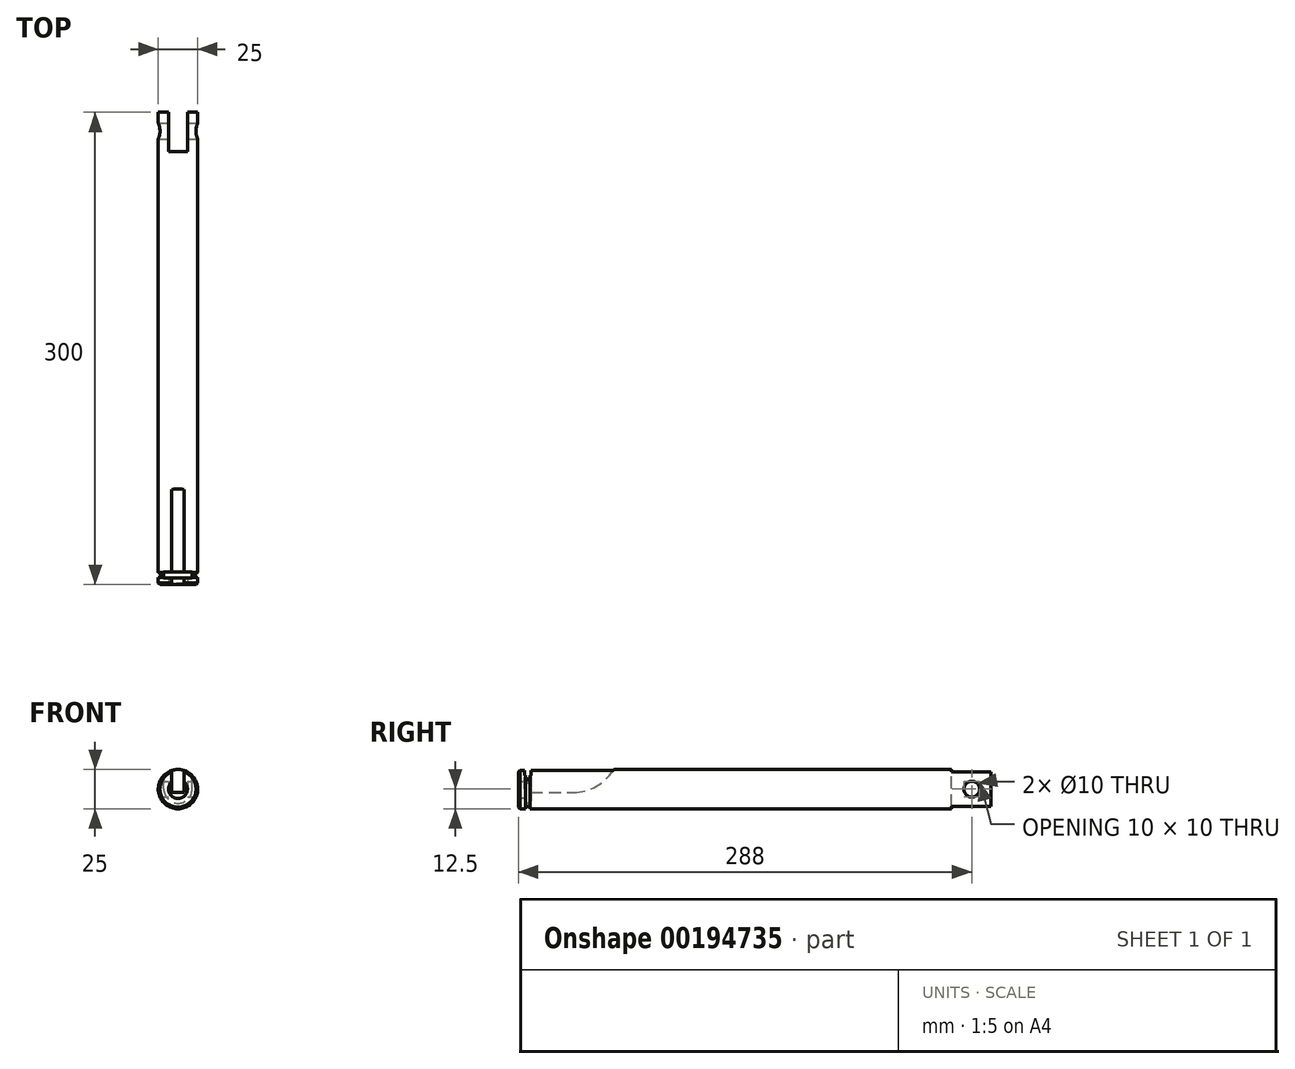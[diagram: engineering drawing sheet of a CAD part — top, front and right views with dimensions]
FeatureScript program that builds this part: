
annotation { "Feature Type Name" : "Feature", "Feature Type Description" : "" }
export const myFeature = defineFeature(function(context is Context, id is Id, definition is map)
    precondition{}
    {
        {
            var Q0;
            Q0=qCreatedBy(makeId("Front.planeOp"),FACE);
            var sketch = newSketch(context, id + "F0", { "sketchPlane" : qUnion([Q0])});
            skCircle(sketch, "E0", {"center": v(0, 0) * mm, "radius": 12.5 * mm});
            skSolve(sketch);
        }
        {
            var Q0;
            Q0=makeQuery(id+"F0.imprint","IMPRINT",FACE,{"disambiguationData":[TD([[makeQuery(id+"F0.imprint","IMPRINT",EDGE,{"derivedFrom":sQuery(id+"F0.wireOp",EDGE,"E0")}),1.0]])]});
            extrude(context, id + "F1", {"entities" : qUnion([Q0]), "oppositeDirection" : true, "depth" : 300 * mm});
        }
        {
            var Q0;
            Q0=qCreatedBy(makeId("Top.planeOp"),FACE);
            var sketch = newSketch(context, id + "F2", { "sketchPlane" : qUnion([Q0])});
            skLineSegment(sketch, "E1.bottom", {"start": v(6, 325) * mm, "end": v(-6, 325) * mm});
            skLineSegment(sketch, "E1.top", {"start": v(6, 275) * mm, "end": v(-6, 275) * mm});
            skLineSegment(sketch, "E1.left", {"start": v(6, 325) * mm, "end": v(6, 275) * mm});
            skLineSegment(sketch, "E1.right", {"start": v(-6, 325) * mm, "end": v(-6, 275) * mm});
            skPoint(sketch, "E1.middle", {"position": v(0, 300) * mm});
            skSolve(sketch);
        }
        {
            var Q0;
            Q0 = qSketchRegion(id + "F2", true);
            extrude(context, id + "F3", {"entities" : qUnion([Q0]), "operationType" : NewBodyOperationType.REMOVE, "endBound" : BoundingType.THROUGH_ALL, "oppositeDirection" : true, "depth" : 25 * mm, "hasSecondDirection" : true, "secondDirectionBound" : SecondDirectionBoundingType.THROUGH_ALL, "secondDirectionOppositeDirection" : false, "secondDirectionDepth" : 25 * mm});
        }
        {
            var Q0;
            Q0=qCreatedBy(makeId("Right.planeOp"),FACE);
            var sketch = newSketch(context, id + "F4", { "sketchPlane" : qUnion([Q0])});
            skCircle(sketch, "E2", {"center": v(288, 0) * mm, "radius": 5 * mm});
            skSolve(sketch);
        }
        {
            var Q0;
            Q0 = qSketchRegion(id + "F4", true);
            extrude(context, id + "F5", {"entities" : qUnion([Q0]), "operationType" : NewBodyOperationType.REMOVE, "endBound" : BoundingType.THROUGH_ALL, "oppositeDirection" : true, "depth" : 25 * mm, "hasSecondDirection" : true, "secondDirectionBound" : SecondDirectionBoundingType.THROUGH_ALL, "secondDirectionOppositeDirection" : false, "secondDirectionDepth" : 25 * mm});
        }
        {
            var Q0;
            Q0=qCreatedBy(makeId("Right.planeOp"),FACE);
            var sketch = newSketch(context, id + "F6", { "sketchPlane" : qUnion([Q0])});
            skLineSegment(sketch, "E3", {"start": v(0, -2) * mm, "end": v(35, -2) * mm});
            skLineSegment(sketch, "E4", {"start": v(65, 28) * mm, "end": v(65, 43.21) * mm});
            skLineSegment(sketch, "E5", {"start": v(65, 43.21) * mm, "end": v(0, 43.21) * mm});
            skLineSegment(sketch, "E6", {"start": v(0, 43.21) * mm, "end": v(0, -2) * mm});
            skPoint(sketch, "E7.visualSharp", {"position": v(65, -2) * mm});
            skArc(sketch, "E7.filletArc", {"start": v(35, -2) * mm, "mid": v(56.21, 6.79) * mm, "end": v(65, 28) * mm});
            skSolve(sketch);
        }
        {
            var Q0;
            Q0 = qSketchRegion(id + "F6", true);
            extrude(context, id + "F7", {"entities" : qUnion([Q0]), "operationType" : NewBodyOperationType.REMOVE, "depth" : 4 * mm, "hasSecondDirection" : true, "secondDirectionOppositeDirection" : true, "secondDirectionDepth" : 4 * mm});
        }
        {
            var Q0;
            Q0=qCreatedBy(makeId("Front.planeOp"),FACE);
            cPlane(context, id + "F8", {"entities" : qUnion([Q0]), "cplaneType" : CPlaneType.OFFSET, "offset" : 6 * mm, "oppositeDirection" : true, "width" : 150 * mm, "height" : 150 * mm});
        }
        {
            var Q0;
            Q0=qCreatedBy(id+"F8.planeOp",FACE);
            var sketch = newSketch(context, id + "F9", { "sketchPlane" : qUnion([Q0])});
            skArc(sketch, "E8", {"start": v(-9, 0) * mm, "mid": v(0, -9) * mm, "end": v(9, 0) * mm});
            skLineSegment(sketch, "E9", {"start": v(-9, 0) * mm, "end": v(-9, 23.97) * mm});
            skLineSegment(sketch, "E10", {"start": v(9, 0) * mm, "end": v(9, 23.97) * mm});
            skLineSegment(sketch, "E11", {"start": v(9, 23.97) * mm, "end": v(-9, 23.97) * mm});
            skSolve(sketch);
        }
        {
            var Q0;
            Q0 = qSketchRegion(id + "F9", true);
            extrude(context, id + "F10", {"entities" : qUnion([Q0]), "operationType" : NewBodyOperationType.REMOVE, "oppositeDirection" : true, "depth" : 2 * mm, "hasSecondDirection" : true, "secondDirectionOppositeDirection" : false, "secondDirectionDepth" : 2 * mm});
        }
        {
            var Q0;
            Q0=qCreatedBy(makeId("Front.planeOp"),FACE);
            var sketch = newSketch(context, id + "F11", { "sketchPlane" : qUnion([Q0])});
            skCircle(sketch, "E12", {"center": v(0, 0) * mm, "radius": 6 * mm});
            skSolve(sketch);
        }
        {
            var Q0;
            Q0 = qSketchRegion(id + "F11", true);
            var Q1;
            Q1=makeQuery(id+"F10.boolean.opBoolean","COPY",FACE,{"derivedFrom":makeQuery(id+"F10.opExtrude","CAP_FACE",FACE,{"disambiguationData":[OSD([sQuery(id+"F9.wireOp",EDGE,"E8"),sQuery(id+"F9.wireOp",EDGE,"E9"),sQuery(id+"F9.wireOp",EDGE,"E10"),sQuery(id+"F9.wireOp",EDGE,"E11")])],"isStart":false})});
            extrude(context, id + "F12", {"entities" : qUnion([Q0]), "operationType" : NewBodyOperationType.REMOVE, "endBound" : BoundingType.UP_TO_SURFACE, "oppositeDirection" : true, "endBoundEntityFace" : qUnion([Q1]), "depth" : 10 * mm});
        }
        {
            var Q0;
            Q0=qCreatedBy(makeId("Top.planeOp"),FACE);
            var sketch = newSketch(context, id + "F13", { "sketchPlane" : qUnion([Q0])});
            skCircle(sketch, "E13", {"center": v(12.5, 6) * mm, "radius": 1.5 * mm});
            skLineSegment(sketch, "E14", {"start": v(0, 0) * mm, "end": v(0, 15.64) * mm, "construction": true});
            skSolve(sketch);
        }
        {
            var Q0;
            Q0 = qSketchRegion(id + "F13", true);
            var Q1;
            Q1=sQuery(id+"F13.wireOp",EDGE,"E14");
            revolve(context, id + "F14", {"operationType" : NewBodyOperationType.REMOVE, "entities" : qUnion([Q0]), "axis" : qUnion([Q1]), "revolveType" : RevolveType.FULL, "oppositeDirection" : true});
        }
        {
            var Q0;
            Q0=makeQuery(id+"F1.opExtrude","CAP_EDGE",EDGE,{"disambiguationData":[OSD([sQuery(id+"F0.wireOp",EDGE,"E0")])],"isStart":true});
            chamfer(context, id + "F15", {"entities" : qUnion([Q0]), "width" : 1 * mm, "tangentPropagation" : true});
        }
        {
            var Q0;
            Q0=qCreatedBy(makeId("Right.planeOp"),FACE);
            var sketch = newSketch(context, id + "F16", { "sketchPlane" : qUnion([Q0])});
            skLineSegment(sketch, "E15", {"start": v(0, 0) * mm, "end": v(315.7, 0) * mm, "construction": true});
            skSolve(sketch);
        }
        {
            var Q0;
            Q0=qCreatedBy(makeId("Right.planeOp"),FACE);
            var Q1;
            Q1=sQuery(id+"F16.wireOp",EDGE,"E15");
            cPlane(context, id + "F17", {"entities" : qUnion([Q0, Q1]), "cplaneType" : CPlaneType.LINE_ANGLE, "offset" : 25 * mm, "angle" : 30 * degree, "width" : 150 * mm, "height" : 150 * mm});
        }
        {
            var Q0;
            Q0=qCreatedBy(id+"F17.planeOp",FACE);
            var sketch = newSketch(context, id + "F18", { "sketchPlane" : qUnion([Q0])});
            skCircle(sketch, "E16", {"center": v(-6, 0) * mm, "radius": 1 * mm});
            skSolve(sketch);
        }
        {
            var Q0;
            Q0 = qSketchRegion(id + "F18", true);
            extrude(context, id + "F19", {"entities" : qUnion([Q0]), "operationType" : NewBodyOperationType.REMOVE, "endBound" : BoundingType.THROUGH_ALL, "depth" : 25 * mm});
        }
    });
